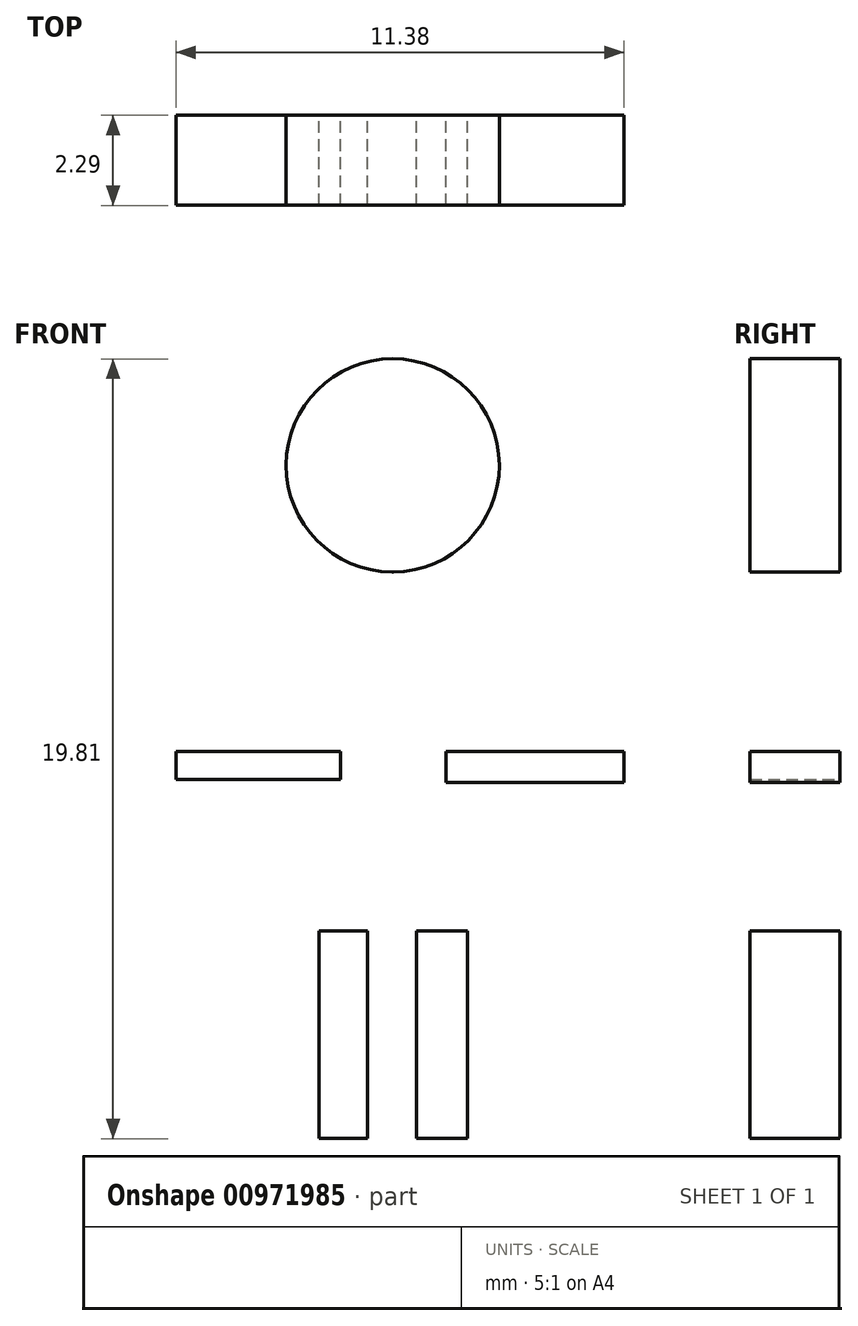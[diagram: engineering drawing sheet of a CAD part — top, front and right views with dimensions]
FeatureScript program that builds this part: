
annotation { "Feature Type Name" : "Feature", "Feature Type Description" : "" }
export const myFeature = defineFeature(function(context is Context, id is Id, definition is map)
    precondition{}
    {
        {
            var Q0;
            Q0=qCreatedBy(makeId("Front.planeOp"),FACE);
            var sketch = newSketch(context, id + "F0", { "sketchPlane" : qUnion([Q0])});
            skLineSegment(sketch, "E0.bottom", {"start": v(1.34, -4.56) * mm, "end": v(-1.34, -4.56) * mm});
            skLineSegment(sketch, "E0.top", {"start": v(1.34, 4.56) * mm, "end": v(-1.34, 4.56) * mm});
            skLineSegment(sketch, "E0.left", {"start": v(1.34, -4.56) * mm, "end": v(1.34, 4.56) * mm});
            skLineSegment(sketch, "E0.right", {"start": v(-1.34, -4.56) * mm, "end": v(-1.34, 4.56) * mm});
            skPoint(sketch, "E0.middle", {"position": v(0, 0) * mm});
            skPoint(sketch, "E1", {"position": v(0, 4.56) * mm});
            skPoint(sketch, "E2", {"position": v(-0.65, -4.56) * mm});
            skPoint(sketch, "E3", {"position": v(0.58, -4.56) * mm});
            skLineSegment(sketch, "E4.bottom", {"start": v(-0.65, -4.56) * mm, "end": v(-1.89, -4.56) * mm});
            skLineSegment(sketch, "E4.top", {"start": v(-0.65, -9.84) * mm, "end": v(-1.89, -9.84) * mm});
            skLineSegment(sketch, "E4.left", {"start": v(-0.65, -4.56) * mm, "end": v(-0.65, -9.84) * mm});
            skLineSegment(sketch, "E4.right", {"start": v(-1.89, -4.56) * mm, "end": v(-1.89, -9.84) * mm});
            skLineSegment(sketch, "E5.bottom", {"start": v(0.58, -4.56) * mm, "end": v(1.89, -4.56) * mm});
            skLineSegment(sketch, "E5.top", {"start": v(0.58, -9.84) * mm, "end": v(1.89, -9.84) * mm});
            skLineSegment(sketch, "E5.left", {"start": v(0.58, -4.56) * mm, "end": v(0.58, -9.84) * mm});
            skLineSegment(sketch, "E5.right", {"start": v(1.89, -4.56) * mm, "end": v(1.89, -9.84) * mm});
            skCircle(sketch, "E6", {"center": v(-0.02, 7.27) * mm, "radius": 2.7 * mm});
            skPoint(sketch, "E6.second.point", {"position": v(0, 9.97) * mm});
            skPoint(sketch, "E6.third.point", {"position": v(2.16, 8.88) * mm});
            skPoint(sketch, "E7", {"position": v(-1.34, 0) * mm});
            skPoint(sketch, "E8", {"position": v(1.34, 0) * mm});
            skLineSegment(sketch, "E9.bottom", {"start": v(-1.34, 0) * mm, "end": v(-5.52, 0) * mm});
            skLineSegment(sketch, "E9.top", {"start": v(-1.34, -0.72) * mm, "end": v(-5.52, -0.72) * mm});
            skLineSegment(sketch, "E9.left", {"start": v(-1.34, 0) * mm, "end": v(-1.34, -0.72) * mm});
            skLineSegment(sketch, "E9.right", {"start": v(-5.52, 0) * mm, "end": v(-5.52, -0.72) * mm});
            skLineSegment(sketch, "E10.bottom", {"start": v(1.34, 0) * mm, "end": v(5.86, 0) * mm});
            skLineSegment(sketch, "E10.top", {"start": v(1.34, -0.79) * mm, "end": v(5.86, -0.79) * mm});
            skLineSegment(sketch, "E10.left", {"start": v(1.34, 0) * mm, "end": v(1.34, -0.79) * mm});
            skLineSegment(sketch, "E10.right", {"start": v(5.86, 0) * mm, "end": v(5.86, -0.79) * mm});
            skLineSegment(sketch, "E11", {"start": v(0, 9.97) * mm, "end": v(0, -9.84) * mm});
            skSolve(sketch);
        }
        {
            var Q0;
            {var subQ0=sQuery(id+"F0.wireOp",EDGE,"E11");var subQ1=sQuery(id+"F0.wireOp",EDGE,"E6");var subQ2=makeQuery(id+"F0.imprint","INTERSECT",VERTEX,{"derivedFrom":[subQ1,subQ0]});Q0=makeQuery(id+"F0.imprint","IMPRINT",FACE,{"disambiguationData":[TD([[makeQuery(id+"F0.imprint","IMPRINT",EDGE,{"disambiguationData":[TD([[subQ2,-1.0]])],"derivedFrom":subQ1}),1.0]])]});}
            var Q1;
            {var subQ0=sQuery(id+"F0.wireOp",EDGE,"E11");var subQ1=sQuery(id+"F0.wireOp",EDGE,"E6");var subQ2=makeQuery(id+"F0.imprint","INTERSECT",VERTEX,{"derivedFrom":[subQ1,subQ0]});Q1=makeQuery(id+"F0.imprint","IMPRINT",FACE,{"disambiguationData":[TD([[makeQuery(id+"F0.imprint","IMPRINT",EDGE,{"disambiguationData":[TD([[subQ2,1.0]])],"derivedFrom":subQ1}),1.0]])]});}
            var Q2;
            {var subQ3=sQuery(id+"F0.wireOp",EDGE,"E9.left");Q2=makeQuery(id+"F0.imprint","IMPRINT",FACE,{"disambiguationData":[TD([[makeQuery(id+"F0.imprint","IMPRINT",EDGE,{"derivedFrom":subQ3}),1.0]])]});}
            var Q3;
            Q3=makeQuery(id+"F0.imprint","IMPRINT",FACE,{"disambiguationData":[TD([[makeQuery(id+"F0.imprint","IMPRINT",EDGE,{"derivedFrom":sQuery(id+"F0.wireOp",EDGE,"E4.top")}),-1.0]])]});
            var Q4;
            Q4=makeQuery(id+"F0.imprint","IMPRINT",FACE,{"disambiguationData":[TD([[makeQuery(id+"F0.imprint","IMPRINT",EDGE,{"derivedFrom":sQuery(id+"F0.wireOp",EDGE,"E5.top")}),1.0]])]});
            var Q5;
            {var subQ3=sQuery(id+"F0.wireOp",EDGE,"E10.left");Q5=makeQuery(id+"F0.imprint","IMPRINT",FACE,{"disambiguationData":[TD([[makeQuery(id+"F0.imprint","IMPRINT",EDGE,{"derivedFrom":subQ3}),-1.0]])]});}
            var Q6;
            Q6=makeQuery(id+"F0.imprint","IMPRINT",FACE,{"disambiguationData":[TD([[makeQuery(id+"F0.imprint","IMPRINT",EDGE,{"derivedFrom":sQuery(id+"F0.wireOp",EDGE,"E10.bottom")}),-1.0]])]});
            var Q7;
            Q7=makeQuery(id+"F0.imprint","IMPRINT",FACE,{"disambiguationData":[TD([[makeQuery(id+"F0.imprint","IMPRINT",EDGE,{"derivedFrom":sQuery(id+"F0.wireOp",EDGE,"E9.bottom")}),1.0]])]});
            extrude(context, id + "F1", {"entities" : qUnion([Q0, Q1, Q2, Q3, Q4, Q5, Q6, Q7]), "depth" : 2.3 * mm, "offsetDistance" : 25.4 * mm});
        }
    });
